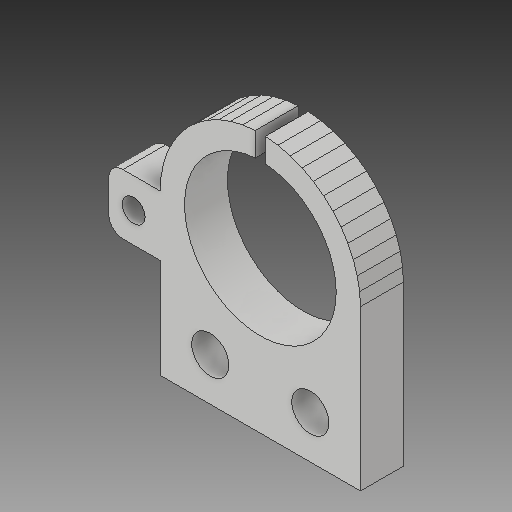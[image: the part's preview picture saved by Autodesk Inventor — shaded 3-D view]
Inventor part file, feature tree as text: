
AUTODESK INVENTOR PART (.ipt)
format: ipt  version: 2018 (Build 220112000, 112)  size: 206,848 bytes
history: native  units: mm
features: sketch x2, extrude x1, hole x1
ambient origin geometry x8: Origin, YZ Plane, XZ Plane, XY Plane, X Axis, Y Axis, Z Axis, Center Point
bodies: Solid1 (feature_tree)
feature tree (4):
  extrude  "Extrusion1"  [1 undecoded]
  hole  "Hole1"  [1 undecoded]
  sketch  "Sketch1"  dims[d0=6.0mm d1=0.0mm]
  sketch  "Sketch3"  dims[d2=21.2mm d3=6.0mm d4=4.0mm d5=2.0mm d6=90.0deg d7=8.0mm d8=20.594885mm]
note: 2 required parameter values undecoded (feature->parameter linkage not recoverable at this tier; creation-order binding heuristic only, values carry confidence <= 0.55)
